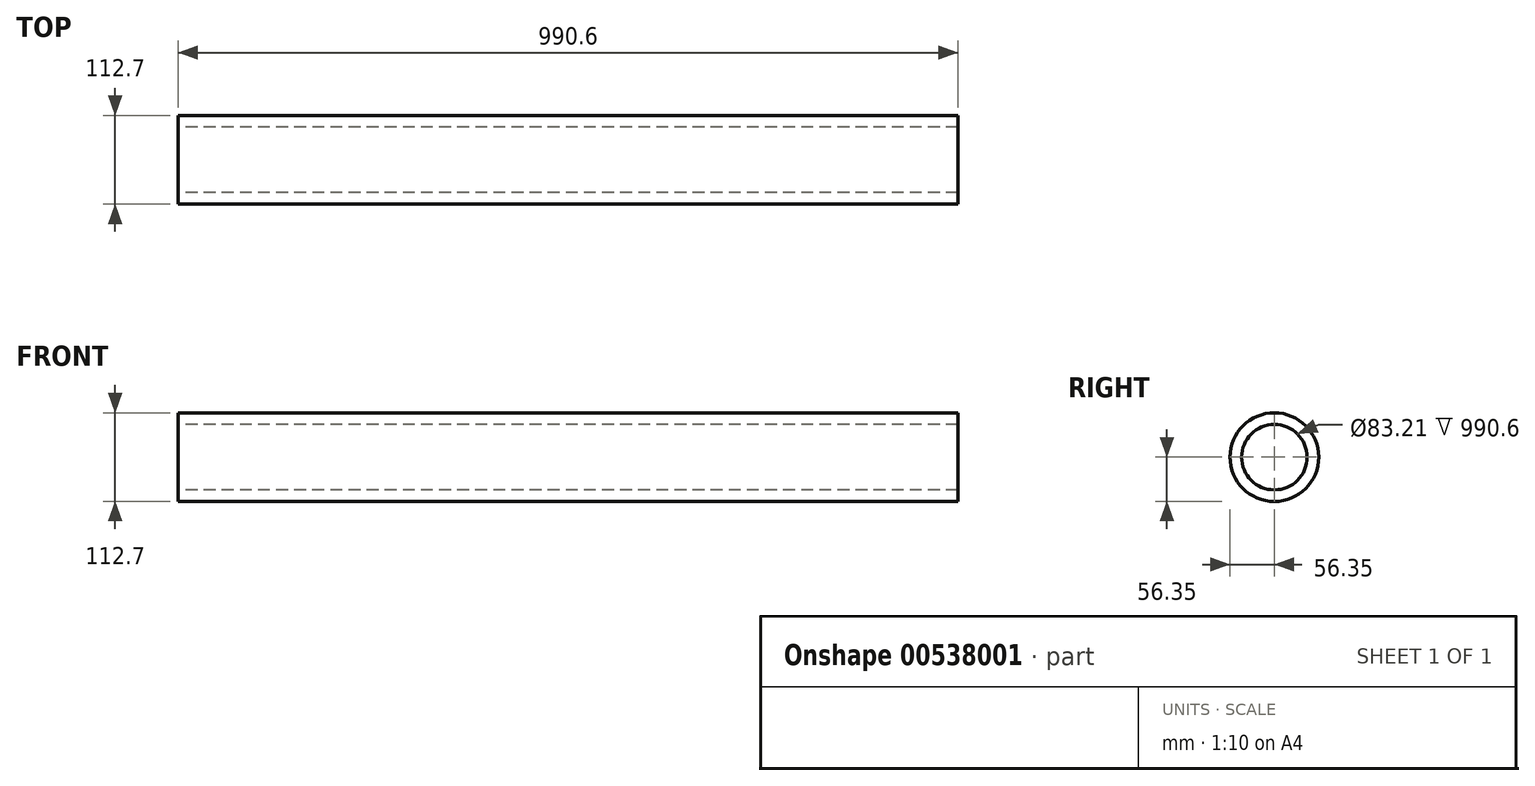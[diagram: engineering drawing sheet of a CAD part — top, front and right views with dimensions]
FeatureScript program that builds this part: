
annotation { "Feature Type Name" : "Feature", "Feature Type Description" : "" }
export const myFeature = defineFeature(function(context is Context, id is Id, definition is map)
    precondition{}
    {
        {
            var Q0;
            Q0=qCreatedBy(makeId("Right.planeOp"),FACE);
            var sketch = newSketch(context, id + "F0", { "sketchPlane" : qUnion([Q0])});
            skCircle(sketch, "E0", {"center": v(0, 0) * mm, "radius": 56.35 * mm});
            skCircle(sketch, "E1", {"center": v(0, 0) * mm, "radius": 41.6 * mm});
            skSolve(sketch);
        }
        {
            var Q0;
            Q0=makeQuery(id+"F0.imprint","IMPRINT",FACE,{"disambiguationData":[TD([[makeQuery(id+"F0.imprint","IMPRINT",EDGE,{"derivedFrom":sQuery(id+"F0.wireOp",EDGE,"E0")}),1.0]])]});
            extrude(context, id + "F1", {"entities" : qUnion([Q0]), "depth" : 990.6 * mm, "offsetDistance" : 25.4 * mm});
        }
    });
